# Revit family: Haworth_BeHold_Modular_Pedestal
name_source: partatom
category: Furniture Systems
revit_build: Autodesk Revit 2018 (Build: 20170223_1515(x64)
units: mm (PartAtom-declared; Revit-internal decimal feet)

## family parameters
Always vertical = Yes
Cut with Voids When Loaded = No
OmniClass Number = 23.40.70.14.64.21
OmniClass Title = Systems Furniture
Part Type = Normal
Room Calculation Point = No
Round Connector Dimension = Use Diameter
Shared = No
Work Plane-Based = No

## types (6) — shared parameters
16d Leg = No
Actual Leg Control = No
Actual Width = 15"
Assembly Code = E2020200
Blade Pull = Yes
Blade Pull Length = 14 13/16"
Case Edge Finish = Haworth _ Laminate _ Beige H-34
Case Finish = Haworth _ Laminate _ Beige H-34
Case Thickness = 3/4"
Caster Back Offset = 1 3/16"
Caster Finish = Haworth _ Polymer _ Slate
Caster Front Offset = 1 7/8"
Casters Side Offset = 1 9/16"
Classic Pull = No
Classic Pull Length = 6 3/4"
Cresent Pull = No
Custom Size = No
Description = Haworth - Be_Hold - Pedestal
Drawer Width = 14 7/8"
Front Edge Finish = Haworth _ Laminate _ Beige H-34
Front Finish = Haworth _ Laminate _ Beige H-34
Glide Finish = Haworth _ Polymer _ Slate
Leg Finish = Haworth _ Paint _ Sky Blue
Leg Height = 6"
Linear Pull = No
Linear Pull Length = 8"
Manufacturer = Haworth
Max. Height = 28"
Max. Width = 15"
Min. Height = 22"
Min. Width = 15"
Model = Haworth Be_Hold
Pull Finish = Haworth _ Paint _ Smooth Plaster
Revision Number = 1
Size = Verify Final Dim. w/ Haworth
Sustainability Info = https://www.haworth.com
Top Thickness = 3/4"
Trim Finish = Haworth _ Paint _ Smooth Plaster
URL = www.haworth.com
URL - Product = http://www.haworth.com
Warranty = http://www.haworth.com
Wing Pull = No
Wing Pull Length = 8 5/16"
With Leg = No
With Lock = Yes

## per-type parameters (varying)
- Attached - B/F - Proud Back - 24d: 3 Drawer Control=No; Actual Depth=24"; Actual Height=22"; Attached=Yes; Back Case Back Control=0"; Back Case Side Control=0"; Bottom Case Offset=1/2"; Bottom Drawer Height=13 149/256"; Bottom Drawer Offset=1 3/8"; Box Box File=No; Box File=Yes; Depth=24"; Distance Between Drawer=1/8"; File File=No; Glide Control=Yes; Inset Style=No; Max. Depth=24"; Middle Drawer Height=6 203/256"; Min. Depth=16"; Mobile=No; Proud Style=Yes; Side Case Back Control=3/4"; Standard Depths=16, 24 in.; Standard Storage Height=22"; Top Case Back Control=0"; Top Drawer Height=6 203/256"; Total Drawer Height=20 1/2"
- Attached - B/B/F - Proud Back - 30d: 3 Drawer Control=Yes; Actual Depth=30"; Actual Height=28"; Attached=Yes; Back Case Back Control=0"; Back Case Side Control=0"; Bottom Case Offset=1/2"; Bottom Drawer Height=13 1/8"; Bottom Drawer Offset=1 3/8"; Box Box File=Yes; Box File=No; Depth=30"; Distance Between Drawer=1/4"; File File=No; Glide Control=Yes; Inset Style=No; Max. Depth=30"; Middle Drawer Height=6 9/16"; Min. Depth=16"; Mobile=No; Proud Style=Yes; Side Case Back Control=3/4"; Standard Depths=16, 18, 24, 30 in.; Standard Storage Height=28"; Top Case Back Control=0"; Top Drawer Height=6 9/16"; Total Drawer Height=26 1/2"
- Attached - F/F - Proud Back - 30d: 3 Drawer Control=No; Actual Depth=30"; Actual Height=28"; Attached=Yes; Back Case Back Control=0"; Back Case Side Control=0"; Bottom Case Offset=1/2"; Bottom Drawer Height=13 3/16"; Bottom Drawer Offset=1 3/8"; Box Box File=No; Box File=No; Depth=30"; Distance Between Drawer=1/8"; File File=Yes; Glide Control=Yes; Inset Style=No; Max. Depth=30"; Middle Drawer Height=6 19/32"; Min. Depth=16"; Mobile=No; Proud Style=Yes; Side Case Back Control=3/4"; Standard Depths=16, 18, 24, 30 in.; Standard Storage Height=28"; Top Case Back Control=0"; Top Drawer Height=13 3/16"; Total Drawer Height=26 1/2"
- Mobile - B/F - Inset Back - 24d: 3 Drawer Control=No; Actual Depth=24"; Actual Height=22"; Attached=No; Back Case Back Control=3/16"; Back Case Side Control=3/4"; Bottom Case Offset=1 3/4"; Bottom Drawer Height=12 3/4"; Bottom Drawer Offset=2 5/8"; Box Box File=No; Box File=Yes; Depth=24"; Distance Between Drawer=1/8"; File File=No; Glide Control=No; Inset Style=Yes; Max. Depth=24"; Middle Drawer Height=6 3/8"; Min. Depth=18"; Mobile=Yes; Proud Style=No; Side Case Back Control=0"; Standard Depths=18, 24 in.; Standard Storage Height=22"; Top Case Back Control=3/16"; Top Drawer Height=6 3/8"; Total Drawer Height=19 1/4"
- Mobile - B/B/F - Inset Back - 24d: 3 Drawer Control=Yes; Actual Depth=24"; Actual Height=28"; Attached=No; Back Case Back Control=3/16"; Back Case Side Control=3/4"; Bottom Case Offset=1 3/4"; Bottom Drawer Height=12 1/2"; Bottom Drawer Offset=2 5/8"; Box Box File=Yes; Box File=No; Depth=24"; Distance Between Drawer=1/4"; File File=No; Glide Control=No; Inset Style=Yes; Max. Depth=24"; Middle Drawer Height=6 1/4"; Min. Depth=18"; Mobile=Yes; Proud Style=No; Side Case Back Control=0"; Standard Depths=18, 24 in.; Standard Storage Height=28"; Top Case Back Control=3/16"; Top Drawer Height=6 1/4"; Total Drawer Height=25 1/4"
- Mobile - F/F - Inset Back - 24d: 3 Drawer Control=No; Actual Depth=24"; Actual Height=28"; Attached=No; Back Case Back Control=3/16"; Back Case Side Control=3/4"; Bottom Case Offset=1 3/4"; Bottom Drawer Height=12 9/16"; Bottom Drawer Offset=2 5/8"; Box Box File=No; Box File=No; Depth=24"; Distance Between Drawer=1/8"; File File=Yes; Glide Control=No; Inset Style=Yes; Max. Depth=24"; Middle Drawer Height=6 9/32"; Min. Depth=18"; Mobile=Yes; Proud Style=No; Side Case Back Control=0"; Standard Depths=18, 24 in.; Standard Storage Height=28"; Top Case Back Control=3/16"; Top Drawer Height=12 9/16"; Total Drawer Height=25 1/4"

## geometry (parser evidence)
native form markers: Sweep x8
no freeform markers — native parametric forms only
